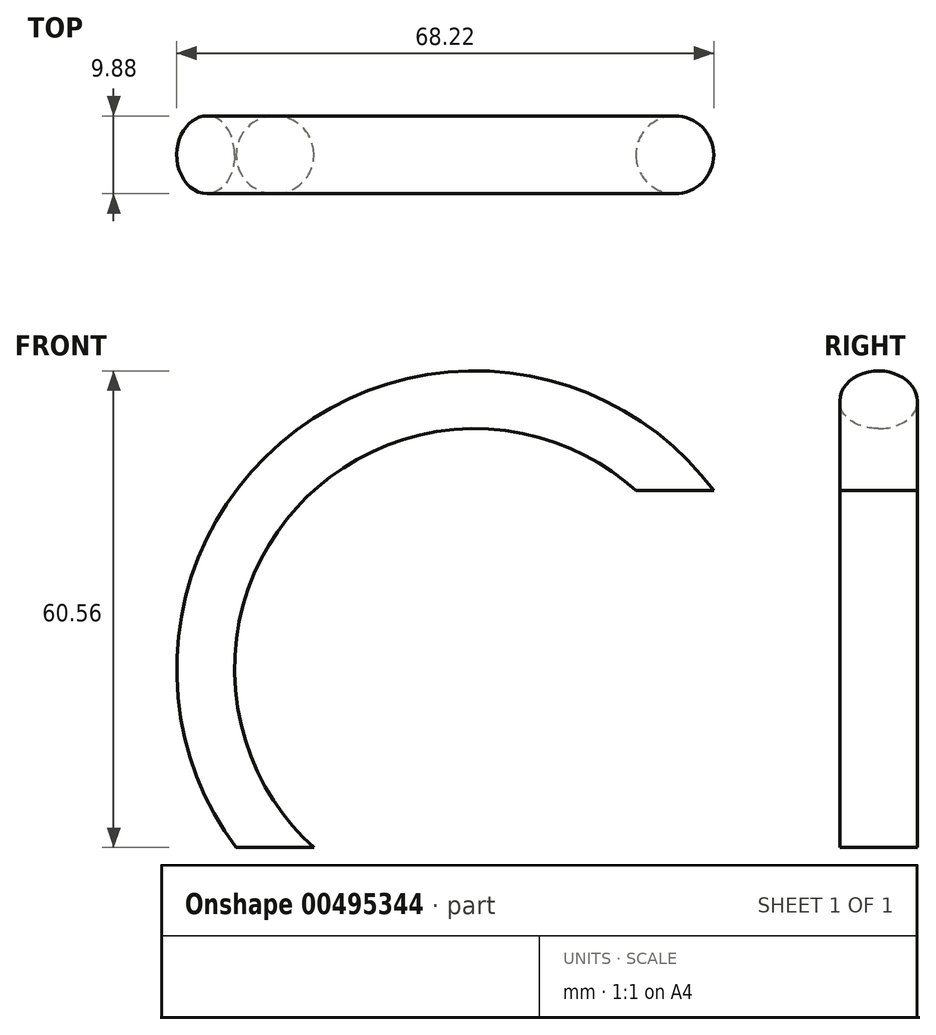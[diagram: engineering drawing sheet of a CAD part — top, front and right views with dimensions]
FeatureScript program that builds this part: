
annotation { "Feature Type Name" : "Feature", "Feature Type Description" : "" }
export const myFeature = defineFeature(function(context is Context, id is Id, definition is map)
    precondition{}
    {
        {
            var Q0;
            Q0=qCreatedBy(makeId("Front.planeOp"),FACE);
            var sketch = newSketch(context, id + "F0", { "sketchPlane" : qUnion([Q0])});
            skLineSegment(sketch, "E0", {"start": v(-25, 0) * mm, "end": v(-25, 22.68) * mm});
            skArc(sketch, "E1", {"start": v(0, 47.68) * mm, "mid": v(-17.68, 40.36) * mm, "end": v(-25, 22.68) * mm});
            skLineSegment(sketch, "E2", {"start": v(0, 55.67) * mm, "end": v(0, -19.07) * mm, "construction": true});
            skArc(sketch, "E3.MirrorCS", {"start": v(0, 47.68) * mm, "mid": v(17.68, 40.36) * mm, "end": v(25, 22.68) * mm});
            skLineSegment(sketch, "E4.MirrorCS", {"start": v(25, 0) * mm, "end": v(25, 22.68) * mm});
            skSolve(sketch);
        }
        {
            var Q0;
            Q0=qCreatedBy(makeId("Top.planeOp"),FACE);
            var sketch = newSketch(context, id + "F1", { "sketchPlane" : qUnion([Q0])});
            skCircle(sketch, "E5", {"center": v(-25.4, 0) * mm, "radius": 4.94 * mm});
            skSolve(sketch);
        }
        {
            var Q0;
            Q0=makeQuery(id+"F1.imprint","IMPRINT",FACE,{"disambiguationData":[TD([[makeQuery(id+"F1.imprint","IMPRINT",EDGE,{"derivedFrom":sQuery(id+"F1.wireOp",EDGE,"E5")}),1.0]])]});
            var Q1;
            Q1=sQuery(id+"F0.wireOp",EDGE,"E1");
            var Q2;
            Q2=sQuery(id+"F0.wireOp",EDGE,"E3.MirrorCS");
            sweep(context, id + "F2", {"profiles" : qUnion([Q0]), "path" : qUnion([Q1, Q2])});
        }
    });
